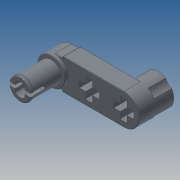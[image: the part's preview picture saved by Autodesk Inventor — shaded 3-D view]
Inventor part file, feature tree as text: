
AUTODESK INVENTOR PART (.ipt)
format: ipt  version: 2022.2 (Build 262287000, 287)  size: 472,064 bytes
history: native  units: mm (DEFAULTED — no unit token found)
features: sketch x6, extrude x5, fillet x2, revolve x1
ambient origin geometry x8: Origin, YZ Plane, XZ Plane, XY Plane, X Axis, Y Axis, Z Axis, Center Point
bodies: Body1 (feature_tree)
feature tree (14):
  revolve  "Revolution1"  [1 undecoded]
  extrude  "Extrusion7"  Depth=8.0mm
  fillet  "Fillet1"  Radius=0.8mm
  extrude  "Extrusion2"  Depth=0.8mm
  extrude  "Extrusion4"  Depth=10.0mm TaperAngle=0.0deg
  extrude  "Extrusion5"  TaperAngle=0.0deg  [1 undecoded]
  extrude  "Extrusion6"  Depth=10.0mm
  fillet  "Fillet3"  Radius=4.8mm
  sketch  "Sketch1"  dims[d1=4.8mm d2=5.0mm]
  sketch  "Sketch2"  dims[d4=0.75mm d6=8.0mm d7=0.8mm]
  sketch  "Sketch4"  dims[d8=6.4mm d9=0.8mm]
  sketch  "Sketch5"  dims[d19=8.0mm d20=90.0deg d25=10.0mm d26=0.0mm]
  sketch  "Sketch6"  dims[d27=0.2mm d28=0.1mm d30=0.0mm]
  sketch  "Sketch7"  dims[d40=135.0deg d41=16.0mm d43=4.8mm d44=1.6mm d45=20.0mm d47=8.0mm d48=10.0mm d50=10.0mm d52=1.6mm d53=4.0mm d54=0.0mm d56=4.0mm d57=0.0mm d58=0.8mm d61=3.0mm d62=0.0mm d65=0.4mm d66=0.1mm d68=2.4mm d69=8.0mm d70=3.2mm d71=0.8mm d72=7.2mm d73=3.2mm d74=45.0deg d75=10.0mm d76=0.0mm d77=3.4mm]
note: 2 required parameter values undecoded (feature->parameter linkage not recoverable at this tier; creation-order binding heuristic only, values carry confidence <= 0.55)